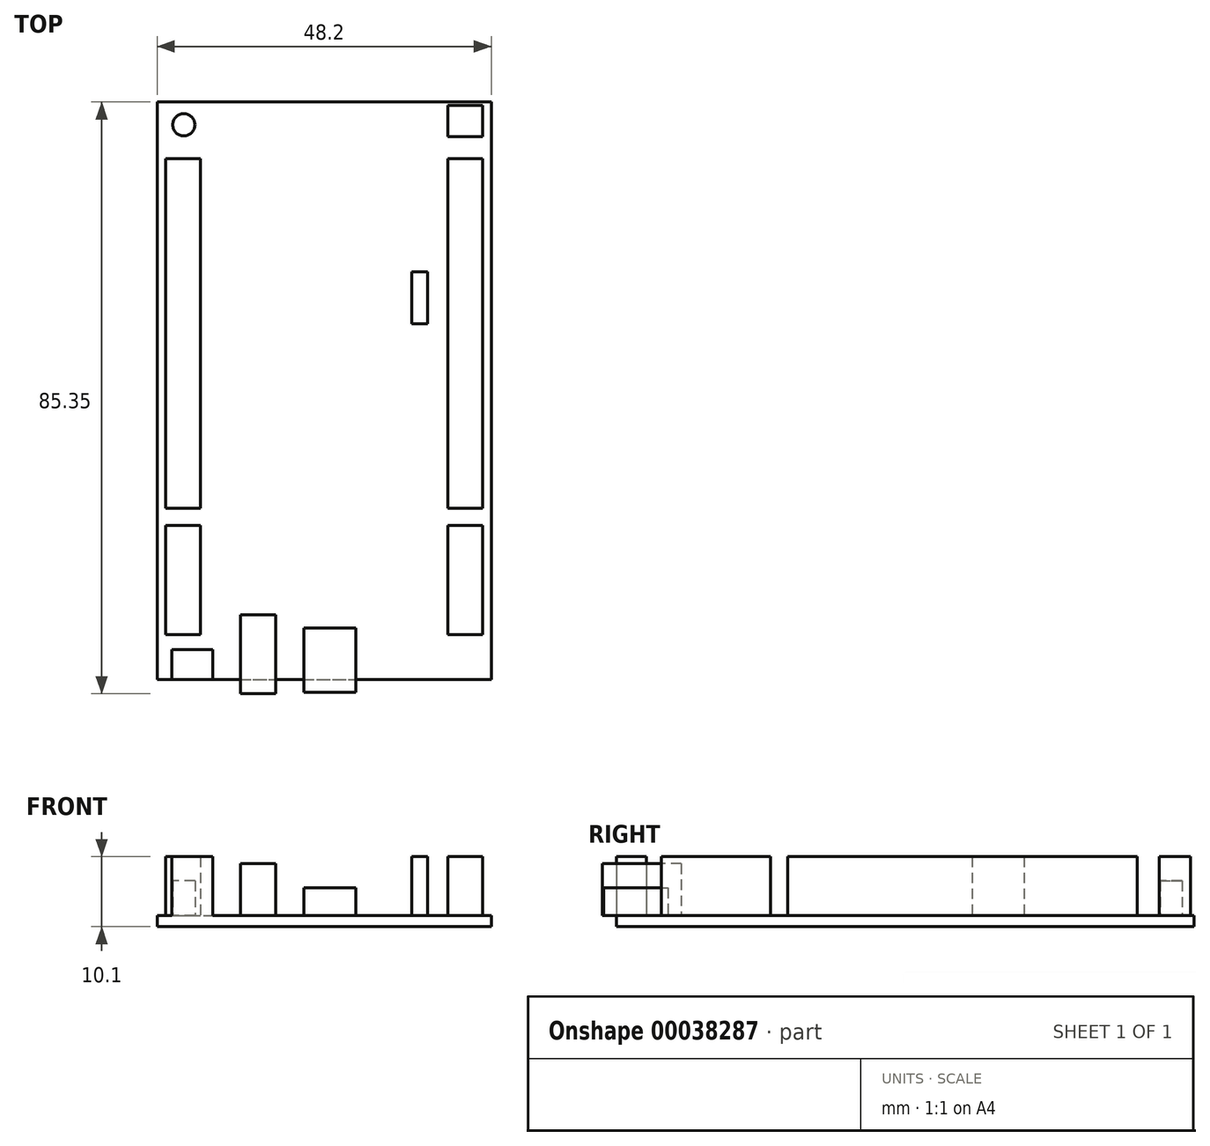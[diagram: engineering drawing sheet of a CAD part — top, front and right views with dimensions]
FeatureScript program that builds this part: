
annotation { "Feature Type Name" : "Feature", "Feature Type Description" : "" }
export const myFeature = defineFeature(function(context is Context, id is Id, definition is map)
    precondition{}
    {
        {
            var Q0;
            Q0=qCreatedBy(makeId("Top.planeOp"),FACE);
            var sketch = newSketch(context, id + "F0", { "sketchPlane" : qUnion([Q0])});
            skLineSegment(sketch, "E0.bottom", {"start": v(0, 0) * mm, "end": v(48.2, 0) * mm});
            skLineSegment(sketch, "E0.top", {"start": v(0, 90.8) * mm, "end": v(48.2, 90.8) * mm});
            skLineSegment(sketch, "E0.left", {"start": v(0, 0) * mm, "end": v(0, 90.8) * mm});
            skLineSegment(sketch, "E0.right", {"start": v(48.2, 0) * mm, "end": v(48.2, 90.8) * mm});
            skLineSegment(sketch, "E1.bottom", {"start": v(10.7, 90.8) * mm, "end": v(37.5, 90.8) * mm});
            skLineSegment(sketch, "E1.top", {"start": v(10.7, 83.3) * mm, "end": v(37.5, 83.3) * mm});
            skLineSegment(sketch, "E1.left", {"start": v(10.7, 90.8) * mm, "end": v(10.7, 83.3) * mm});
            skLineSegment(sketch, "E1.right", {"start": v(37.5, 90.8) * mm, "end": v(37.5, 83.3) * mm});
            skLineSegment(sketch, "E2", {"start": v(0, 83.3) * mm, "end": v(48.2, 83.3) * mm});
            skSolve(sketch);
        }
        {
            var Q0;
            {var subQ3=sQuery(id+"F0.wireOp",EDGE,"E0.bottom");Q0=makeQuery(id+"F0.imprint","IMPRINT",FACE,{"disambiguationData":[TD([[makeQuery(id+"F0.imprint","IMPRINT",EDGE,{"derivedFrom":subQ3}),1.0]])]});}
            var Q1;
            Q1=makeQuery(id+"F0.imprint","IMPRINT",FACE,{"disambiguationData":[TD([[makeQuery(id+"F0.imprint","IMPRINT",EDGE,{"derivedFrom":sQuery(id+"F0.wireOp",EDGE,"E1.bottom")}),-1.0]])]});
            extrude(context, id + "F1", {"entities" : qUnion([Q0, Q1]), "depth" : 1.6 * mm});
        }
        {
            var Q0;
            Q0=makeQuery(id+"F1.opExtrude","CAP_FACE",FACE,{"disambiguationData":[OSD([sQuery(id+"F0.wireOp",EDGE,"E0.bottom"),sQuery(id+"F0.wireOp",EDGE,"E0.left"),sQuery(id+"F0.wireOp",EDGE,"E0.right"),sQuery(id+"F0.wireOp",EDGE,"E1.bottom"),sQuery(id+"F0.wireOp",EDGE,"E1.left"),sQuery(id+"F0.wireOp",EDGE,"E1.right"),sQuery(id+"F0.wireOp",EDGE,"E2")])],"isStart":false});
            var sketch = newSketch(context, id + "F2", { "sketchPlane" : qUnion([Q0])});
            skLineSegment(sketch, "E3.bottom", {"start": v(1.25, 75.1) * mm, "end": v(6.25, 75.1) * mm});
            skLineSegment(sketch, "E3.top", {"start": v(1.25, 24.7) * mm, "end": v(6.25, 24.7) * mm});
            skLineSegment(sketch, "E3.left", {"start": v(1.25, 75.1) * mm, "end": v(1.25, 24.7) * mm});
            skLineSegment(sketch, "E3.right", {"start": v(6.25, 75.1) * mm, "end": v(6.25, 24.7) * mm});
            skLineSegment(sketch, "E4.bottom", {"start": v(41.95, 82.8) * mm, "end": v(46.95, 82.8) * mm});
            skLineSegment(sketch, "E4.top", {"start": v(41.95, 78.3) * mm, "end": v(46.95, 78.3) * mm});
            skLineSegment(sketch, "E4.left", {"start": v(41.95, 82.8) * mm, "end": v(41.95, 78.3) * mm});
            skLineSegment(sketch, "E4.right", {"start": v(46.95, 82.8) * mm, "end": v(46.95, 78.3) * mm});
            skLineSegment(sketch, "E5.bottom", {"start": v(41.95, 75.1) * mm, "end": v(46.95, 75.1) * mm});
            skLineSegment(sketch, "E5.top", {"start": v(41.95, 24.7) * mm, "end": v(46.95, 24.7) * mm});
            skLineSegment(sketch, "E5.left", {"start": v(41.95, 75.1) * mm, "end": v(41.95, 24.7) * mm});
            skLineSegment(sketch, "E5.right", {"start": v(46.95, 75.1) * mm, "end": v(46.95, 24.7) * mm});
            skLineSegment(sketch, "E6.bottom", {"start": v(2.1, 4.3) * mm, "end": v(8, 4.3) * mm});
            skLineSegment(sketch, "E6.top", {"start": v(2.1, 0) * mm, "end": v(8, 0) * mm});
            skLineSegment(sketch, "E6.left", {"start": v(2.1, 4.3) * mm, "end": v(2.1, 0) * mm});
            skLineSegment(sketch, "E6.right", {"start": v(8, 4.3) * mm, "end": v(8, 0) * mm});
            skLineSegment(sketch, "E7.bottom", {"start": v(39, 58.8) * mm, "end": v(36.75, 58.8) * mm});
            skLineSegment(sketch, "E7.top", {"start": v(39, 51.3) * mm, "end": v(36.75, 51.3) * mm});
            skLineSegment(sketch, "E7.left", {"start": v(39, 58.8) * mm, "end": v(39, 51.3) * mm});
            skLineSegment(sketch, "E7.right", {"start": v(36.75, 58.8) * mm, "end": v(36.75, 51.3) * mm});
            skLineSegment(sketch, "E8.bottom", {"start": v(1.25, 22.2) * mm, "end": v(6.25, 22.2) * mm});
            skLineSegment(sketch, "E8.top", {"start": v(1.25, 6.5) * mm, "end": v(6.25, 6.5) * mm});
            skLineSegment(sketch, "E8.left", {"start": v(1.25, 22.2) * mm, "end": v(1.25, 6.5) * mm});
            skLineSegment(sketch, "E8.right", {"start": v(6.25, 22.2) * mm, "end": v(6.25, 6.5) * mm});
            skLineSegment(sketch, "E9.bottom", {"start": v(41.95, 22.2) * mm, "end": v(46.95, 22.2) * mm});
            skLineSegment(sketch, "E9.top", {"start": v(41.95, 6.5) * mm, "end": v(46.95, 6.5) * mm});
            skLineSegment(sketch, "E9.left", {"start": v(41.95, 22.2) * mm, "end": v(41.95, 6.5) * mm});
            skLineSegment(sketch, "E9.right", {"start": v(46.95, 22.2) * mm, "end": v(46.95, 6.5) * mm});
            skSolve(sketch);
        }
        {
            var Q0;
            Q0 = qSketchRegion(id + "F2", true);
            extrude(context, id + "F3", {"entities" : qUnion([Q0]), "operationType" : NewBodyOperationType.ADD, "depth" : 8.5 * mm});
        }
        {
            var Q0;
            Q0=makeQuery(id+"F1.opExtrude","CAP_FACE",FACE,{"disambiguationData":[OSD([sQuery(id+"F0.wireOp",EDGE,"E0.bottom"),sQuery(id+"F0.wireOp",EDGE,"E0.left"),sQuery(id+"F0.wireOp",EDGE,"E0.right"),sQuery(id+"F0.wireOp",EDGE,"E1.bottom"),sQuery(id+"F0.wireOp",EDGE,"E1.left"),sQuery(id+"F0.wireOp",EDGE,"E1.right"),sQuery(id+"F0.wireOp",EDGE,"E2")])],"isStart":false});
            var sketch = newSketch(context, id + "F4", { "sketchPlane" : qUnion([Q0])});
            skLineSegment(sketch, "E10.bottom", {"start": v(21.15, -1.85) * mm, "end": v(28.65, -1.85) * mm});
            skLineSegment(sketch, "E10.top", {"start": v(21.15, 7.4) * mm, "end": v(28.65, 7.4) * mm});
            skLineSegment(sketch, "E10.left", {"start": v(21.15, -1.85) * mm, "end": v(21.15, 7.4) * mm});
            skLineSegment(sketch, "E10.right", {"start": v(28.65, -1.85) * mm, "end": v(28.65, 7.4) * mm});
            skSolve(sketch);
        }
        {
            var Q0;
            Q0 = qSketchRegion(id + "F4", true);
            extrude(context, id + "F5", {"entities" : qUnion([Q0]), "operationType" : NewBodyOperationType.ADD, "depth" : 4 * mm});
        }
        {
            var Q0;
            Q0=makeQuery(id+"F1.opExtrude","CAP_FACE",FACE,{"disambiguationData":[OSD([sQuery(id+"F0.wireOp",EDGE,"E0.bottom"),sQuery(id+"F0.wireOp",EDGE,"E0.left"),sQuery(id+"F0.wireOp",EDGE,"E0.right"),sQuery(id+"F0.wireOp",EDGE,"E1.bottom"),sQuery(id+"F0.wireOp",EDGE,"E1.left"),sQuery(id+"F0.wireOp",EDGE,"E1.right"),sQuery(id+"F0.wireOp",EDGE,"E2")])],"isStart":false});
            var sketch = newSketch(context, id + "F6", { "sketchPlane" : qUnion([Q0])});
            skLineSegment(sketch, "E11.bottom", {"start": v(12.05, 9.35) * mm, "end": v(17.1, 9.35) * mm});
            skLineSegment(sketch, "E11.top", {"start": v(12.05, -2.05) * mm, "end": v(17.1, -2.05) * mm});
            skLineSegment(sketch, "E11.left", {"start": v(12.05, 9.35) * mm, "end": v(12.05, -2.05) * mm});
            skLineSegment(sketch, "E11.right", {"start": v(17.1, 9.35) * mm, "end": v(17.1, -2.05) * mm});
            skSolve(sketch);
        }
        {
            var Q0;
            Q0 = qSketchRegion(id + "F6", true);
            extrude(context, id + "F7", {"entities" : qUnion([Q0]), "operationType" : NewBodyOperationType.ADD, "depth" : 7.5 * mm});
        }
        {
            var Q0;
            Q0=makeQuery(id+"F1.opExtrude","CAP_FACE",FACE,{"disambiguationData":[OSD([sQuery(id+"F0.wireOp",EDGE,"E0.bottom"),sQuery(id+"F0.wireOp",EDGE,"E0.left"),sQuery(id+"F0.wireOp",EDGE,"E0.right"),sQuery(id+"F0.wireOp",EDGE,"E1.bottom"),sQuery(id+"F0.wireOp",EDGE,"E1.left"),sQuery(id+"F0.wireOp",EDGE,"E1.right"),sQuery(id+"F0.wireOp",EDGE,"E2")])],"isStart":false});
            var sketch = newSketch(context, id + "F8", { "sketchPlane" : qUnion([Q0])});
            skCircle(sketch, "E12", {"center": v(3.85, 80) * mm, "radius": 1.6 * mm});
            skSolve(sketch);
        }
        {
            var Q0;
            Q0 = qSketchRegion(id + "F8", true);
            extrude(context, id + "F9", {"entities" : qUnion([Q0]), "operationType" : NewBodyOperationType.ADD, "depth" : 5 * mm});
        }
    });
